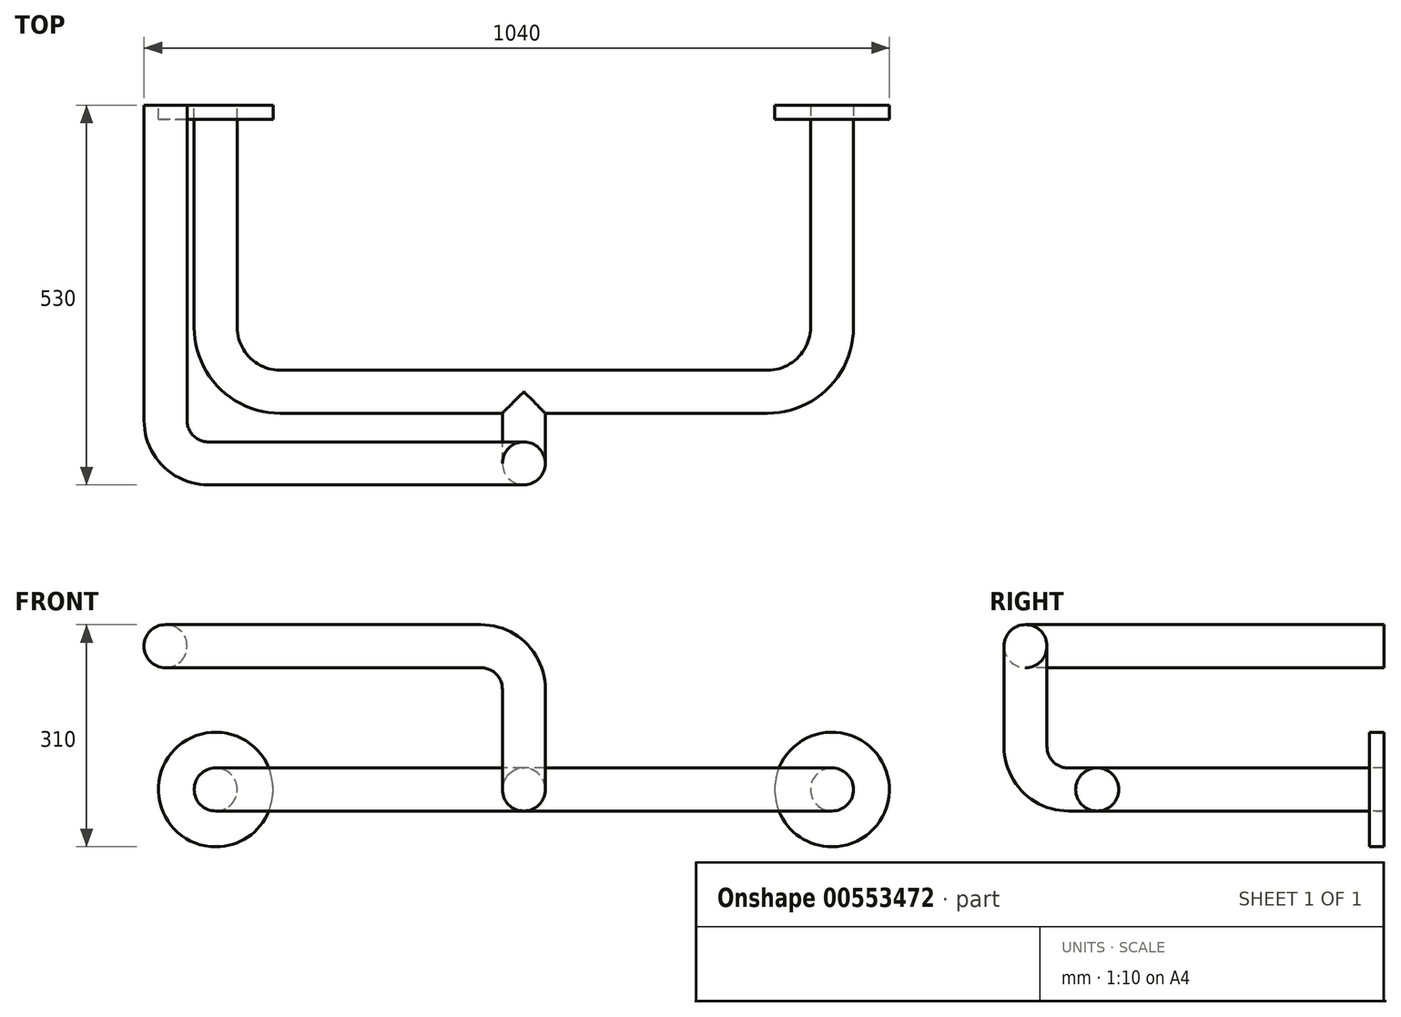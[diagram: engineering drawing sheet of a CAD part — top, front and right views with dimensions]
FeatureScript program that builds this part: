
annotation { "Feature Type Name" : "Feature", "Feature Type Description" : "" }
export const myFeature = defineFeature(function(context is Context, id is Id, definition is map)
    precondition{}
    {
        {
            var Q0;
            Q0=qCreatedBy(makeId("Front.planeOp"),FACE);
            var sketch = newSketch(context, id + "F0", { "sketchPlane" : qUnion([Q0])});
            skCircle(sketch, "E0", {"center": v(0, 0) * mm, "radius": 80 * mm});
            skCircle(sketch, "E1", {"center": v(860, 0) * mm, "radius": 80 * mm});
            skSolve(sketch);
        }
        {
            var Q0;
            Q0=makeQuery(id+"F0.imprint","IMPRINT",FACE,{"disambiguationData":[TD([[makeQuery(id+"F0.imprint","IMPRINT",EDGE,{"derivedFrom":sQuery(id+"F0.wireOp",EDGE,"E0")}),1.0]])]});
            var Q1;
            Q1=makeQuery(id+"F0.imprint","IMPRINT",FACE,{"disambiguationData":[TD([[makeQuery(id+"F0.imprint","IMPRINT",EDGE,{"derivedFrom":sQuery(id+"F0.wireOp",EDGE,"E1")}),1.0]])]});
            extrude(context, id + "F1", {"entities" : qUnion([Q0, Q1]), "depth" : 20 * mm, "offsetDistance" : 25 * mm});
        }
        {
            var Q0;
            Q0=makeQuery(id+"F1.opExtrude","CAP_FACE",FACE,{"disambiguationData":[OSD([sQuery(id+"F0.wireOp",EDGE,"E0")])],"isStart":false});
            var sketch = newSketch(context, id + "F2", { "sketchPlane" : qUnion([Q0])});
            skCircle(sketch, "E2", {"center": v(0, 0) * mm, "radius": 30 * mm});
            skCircle(sketch, "E3", {"center": v(860, 0) * mm, "radius": 30 * mm});
            skSolve(sketch);
        }
        {
            var Q0;
            Q0=qCreatedBy(makeId("Top.planeOp"),FACE);
            var sketch = newSketch(context, id + "F3", { "sketchPlane" : qUnion([Q0])});
            skLineSegment(sketch, "E4", {"start": v(0, 0) * mm, "end": v(0, -310) * mm});
            skLineSegment(sketch, "E5", {"start": v(90, -400) * mm, "end": v(770, -400) * mm});
            skLineSegment(sketch, "E6", {"start": v(860, -310) * mm, "end": v(860, 0) * mm});
            skPoint(sketch, "E7.visualSharp", {"position": v(0, -400) * mm});
            skArc(sketch, "E7.filletArc", {"start": v(0, -310) * mm, "mid": v(26.36, -373.64) * mm, "end": v(90, -400) * mm});
            skPoint(sketch, "E8.visualSharp", {"position": v(860, -400) * mm});
            skArc(sketch, "E8.filletArc", {"start": v(770, -400) * mm, "mid": v(833.64, -373.64) * mm, "end": v(860, -310) * mm});
            skLineSegment(sketch, "E9", {"start": v(430, -400) * mm, "end": v(430, -500) * mm});
            skSolve(sketch);
        }
        {
            var Q0;
            Q0=qCreatedBy(makeId("Right.planeOp"),FACE);
            cPlane(context, id + "F4", {"entities" : qUnion([Q0]), "cplaneType" : CPlaneType.OFFSET, "offset" : (860 / 2) * mm, "width" : 150 * mm, "height" : 150 * mm});
        }
        {
            var Q0;
            Q0=qCreatedBy(id+"F4.planeOp",FACE);
            var sketch = newSketch(context, id + "F5", { "sketchPlane" : qUnion([Q0])});
            skLineSegment(sketch, "E10.0", {"start": v(-400, 0) * mm, "end": v(-440, 0) * mm});
            skLineSegment(sketch, "E11", {"start": v(-500, 60) * mm, "end": v(-500, 200) * mm});
            skPoint(sketch, "E12.visualSharp", {"position": v(-500, 0) * mm});
            skArc(sketch, "E12.filletArc", {"start": v(-500, 60) * mm, "mid": v(-482.43, 17.57) * mm, "end": v(-440, 0) * mm});
            skSolve(sketch);
        }
        {
            var Q0;
            Q0=qCreatedBy(makeId("Front.planeOp"),FACE);
            cPlane(context, id + "F6", {"entities" : qUnion([Q0]), "cplaneType" : CPlaneType.OFFSET, "offset" : 500 * mm, "width" : 150 * mm, "height" : 150 * mm});
        }
        {
            var Q0;
            Q0=qCreatedBy(id+"F6.planeOp",FACE);
            var sketch = newSketch(context, id + "F7", { "sketchPlane" : qUnion([Q0])});
            skLineSegment(sketch, "E13.0", {"start": v(430, 60) * mm, "end": v(430, 140) * mm});
            skLineSegment(sketch, "E14", {"start": v(370, 200) * mm, "end": v(-70, 200) * mm});
            skPoint(sketch, "E15.visualSharp", {"position": v(430, 200) * mm});
            skArc(sketch, "E15.filletArc", {"start": v(430, 140) * mm, "mid": v(412.43, 182.43) * mm, "end": v(370, 200) * mm});
            skSolve(sketch);
        }
        {
            var Q0;
            Q0=qCreatedBy(makeId("Top.planeOp"),FACE);
            cPlane(context, id + "F8", {"entities" : qUnion([Q0]), "cplaneType" : CPlaneType.OFFSET, "offset" : 200 * mm, "width" : 150 * mm, "height" : 150 * mm});
        }
        {
            var Q0;
            Q0=qCreatedBy(id+"F8.planeOp",FACE);
            var sketch = newSketch(context, id + "F9", { "sketchPlane" : qUnion([Q0])});
            skLineSegment(sketch, "E16.0", {"start": v(370, -500) * mm, "end": v(-10, -500) * mm});
            skLineSegment(sketch, "E17", {"start": v(-70, -440) * mm, "end": v(-70, 0) * mm});
            skPoint(sketch, "E18.visualSharp", {"position": v(-70, -500) * mm});
            skArc(sketch, "E18.filletArc", {"start": v(-70, -440) * mm, "mid": v(-52.43, -482.43) * mm, "end": v(-10, -500) * mm});
            skSolve(sketch);
        }
        {
            var Q0;
            Q0=makeQuery(id+"F2.imprint","IMPRINT",FACE,{"disambiguationData":[TD([[makeQuery(id+"F2.imprint","IMPRINT",EDGE,{"derivedFrom":sQuery(id+"F2.wireOp",EDGE,"E3")}),1.0]])]});
            var Q1;
            Q1=sQuery(id+"F3.wireOp",EDGE,"E6");
            var Q2;
            Q2=sQuery(id+"F3.wireOp",EDGE,"E8.filletArc");
            var Q3;
            Q3=sQuery(id+"F3.wireOp",EDGE,"E5");
            var Q4;
            Q4=sQuery(id+"F3.wireOp",EDGE,"E7.filletArc");
            var Q5;
            Q5=sQuery(id+"F3.wireOp",EDGE,"E4");
            sweep(context, id + "F10", {"profiles" : qUnion([Q0]), "path" : qUnion([Q1, Q2, Q3, Q4, Q5])});
        }
        {
            var Q0;
            Q0=qCreatedBy(makeId("Front.planeOp"),FACE);
            var sketch = newSketch(context, id + "F11", { "sketchPlane" : qUnion([Q0])});
            skCircle(sketch, "E19", {"center": v(-70, 200) * mm, "radius": 30 * mm});
            skSolve(sketch);
        }
        {
            var Q0;
            Q0=makeQuery(id+"F11.imprint","IMPRINT",FACE,{"disambiguationData":[TD([[makeQuery(id+"F11.imprint","IMPRINT",EDGE,{"derivedFrom":sQuery(id+"F11.wireOp",EDGE,"E19")}),1.0]])]});
            var Q1;
            Q1=sQuery(id+"F9.wireOp",EDGE,"E17");
            var Q2;
            Q2=sQuery(id+"F9.wireOp",EDGE,"E18.filletArc");
            var Q3;
            Q3=sQuery(id+"F9.wireOp",EDGE,"E16.0");
            var Q4;
            Q4=sQuery(id+"F7.wireOp",EDGE,"E15.filletArc");
            var Q5;
            Q5=sQuery(id+"F7.wireOp",EDGE,"E13.0");
            var Q6;
            Q6=sQuery(id+"F5.wireOp",EDGE,"E10.0");
            var Q7;
            Q7=sQuery(id+"F5.wireOp",EDGE,"E12.filletArc");
            sweep(context, id + "F12", {"operationType" : NewBodyOperationType.ADD, "profiles" : qUnion([Q0]), "path" : qUnion([Q1, Q2, Q3, Q4, Q5, Q6, Q7])});
        }
    });
